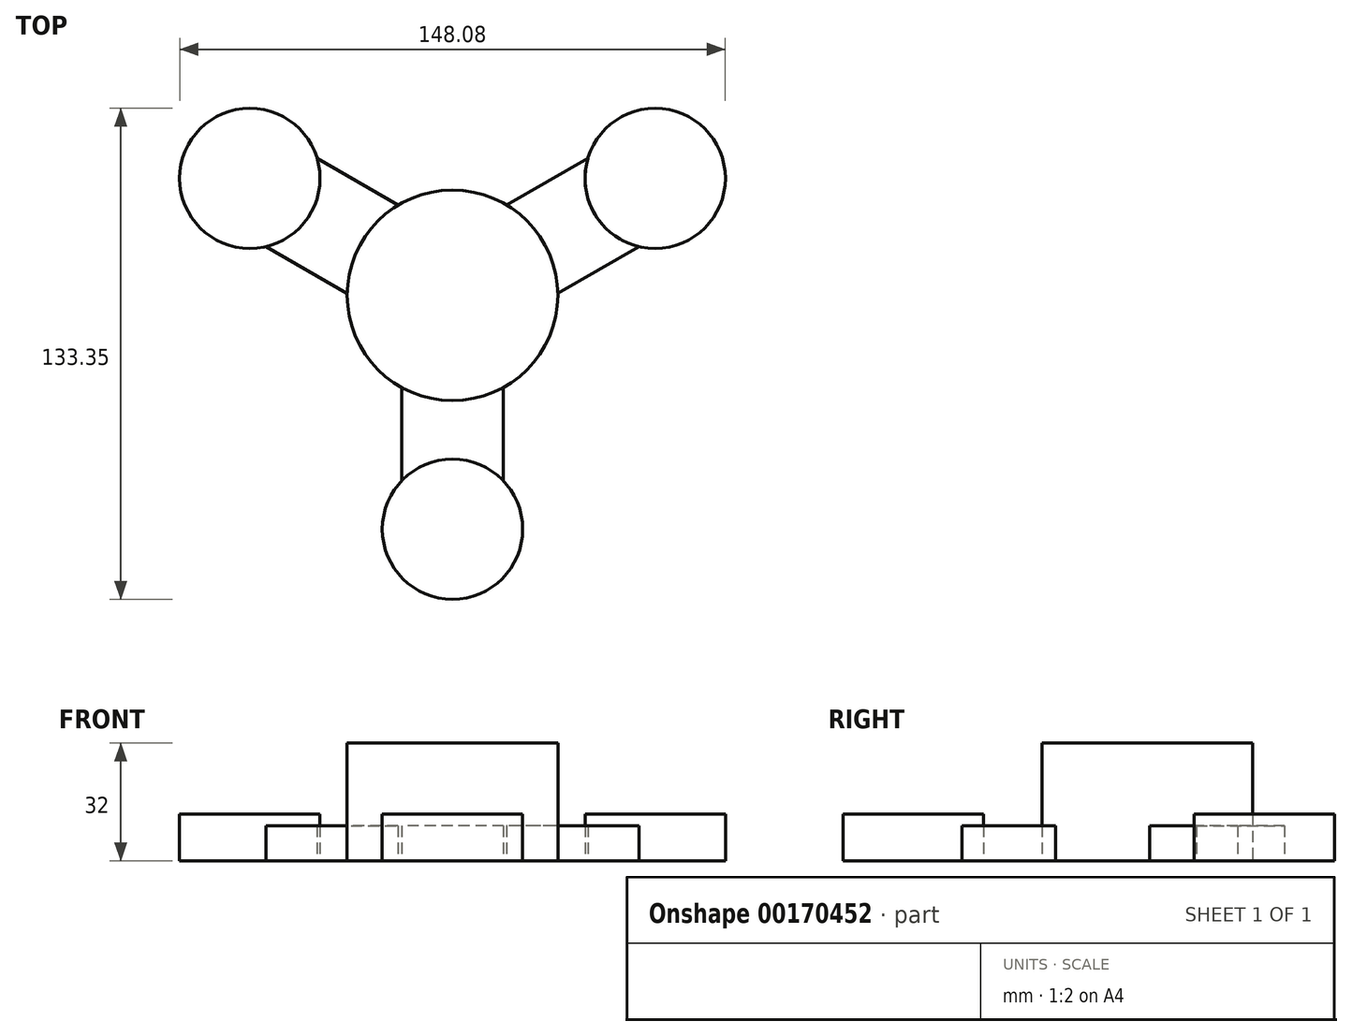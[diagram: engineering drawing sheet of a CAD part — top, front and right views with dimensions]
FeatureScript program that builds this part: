
annotation { "Feature Type Name" : "Feature", "Feature Type Description" : "" }
export const myFeature = defineFeature(function(context is Context, id is Id, definition is map)
    precondition{}
    {
        {
            var Q0;
            Q0=qCreatedBy(makeId("Top.planeOp"),FACE);
            var sketch = newSketch(context, id + "F0", { "sketchPlane" : qUnion([Q0])});
            skCircle(sketch, "E0", {"center": v(0, 0) * mm, "radius": 28.58 * mm});
            skLineSegment(sketch, "E1", {"start": v(0, 0) * mm, "end": v(-55, 31.75) * mm});
            skCircle(sketch, "E2", {"center": v(-55, 31.75) * mm, "radius": 19.05 * mm});
            skLineSegment(sketch, "E3", {"start": v(-55, 31.75) * mm, "end": v(-64.52, 15.25) * mm});
            skLineSegment(sketch, "E4", {"start": v(-55, 31.75) * mm, "end": v(-45.47, 48.25) * mm});
            skLineSegment(sketch, "E5", {"start": v(-36.73, 37.18) * mm, "end": v(-14.74, 24.48) * mm});
            skLineSegment(sketch, "E6.MirrorCS", {"start": v(-50.57, 13.22) * mm, "end": v(-28.57, 0.52) * mm});
            skSolve(sketch);
        }
        {
            var Q0;
            {var subQ0=sQuery(id+"F0.wireOp",EDGE,"E3");Q0=makeQuery(id+"F0.imprint","IMPRINT",FACE,{"disambiguationData":[TD([[makeQuery(id+"F0.imprint","IMPRINT",EDGE,{"derivedFrom":subQ0}),-1.0]])]});}
            var Q1;
            {var subQ0=sQuery(id+"F0.wireOp",EDGE,"E4");Q1=makeQuery(id+"F0.imprint","IMPRINT",FACE,{"disambiguationData":[TD([[makeQuery(id+"F0.imprint","IMPRINT",EDGE,{"derivedFrom":subQ0}),-1.0]])]});}
            var Q2;
            {var subQ0=sQuery(id+"F0.wireOp",EDGE,"E3");Q2=makeQuery(id+"F0.imprint","IMPRINT",FACE,{"disambiguationData":[TD([[makeQuery(id+"F0.imprint","IMPRINT",EDGE,{"derivedFrom":subQ0}),1.0]])]});}
            extrude(context, id + "F1", {"entities" : qUnion([Q0, Q1, Q2]), "depth" : 12.7 * mm, "offsetDistance" : 25.4 * mm});
        }
        {
            var Q0;
            {var subQ0=sQuery(id+"F0.wireOp",EDGE,"E0");var subQ1=makeQuery(id+"F0.imprint","INTERSECT",VERTEX,{"derivedFrom":[subQ0,sQuery(id+"F0.wireOp",EDGE,"E5")]});Q0=makeQuery(id+"F0.imprint","IMPRINT",FACE,{"disambiguationData":[TD([[makeQuery(id+"F0.imprint","IMPRINT",EDGE,{"disambiguationData":[TD([[subQ1,-1.0]])],"derivedFrom":subQ0}),1.0]])]});}
            extrude(context, id + "F2", {"entities" : qUnion([Q0]), "depth" : 19.05 * mm, "offsetDistance" : 25.4 * mm});
        }
        {
            var Q0;
            {var subQ0=sQuery(id+"F0.wireOp",EDGE,"E5");Q0=makeQuery(id+"F0.imprint","IMPRINT",FACE,{"disambiguationData":[TD([[makeQuery(id+"F0.imprint","IMPRINT",EDGE,{"derivedFrom":subQ0}),-1.0]])]});}
            var Q1;
            {var subQ0=sQuery(id+"F0.wireOp",EDGE,"E6.MirrorCS");Q1=makeQuery(id+"F0.imprint","IMPRINT",FACE,{"disambiguationData":[TD([[makeQuery(id+"F0.imprint","IMPRINT",EDGE,{"derivedFrom":subQ0}),1.0]])]});}
            extrude(context, id + "F3", {"entities" : qUnion([Q0, Q1]), "depth" : 9.52 * mm, "offsetDistance" : 25.4 * mm});
        }
        {
            var Q0;
            Q0=makeQuery(id+"F1.opExtrude","SWEPT_BODY",BODY,{"disambiguationData":[OSD([sQuery(id+"F0.wireOp",EDGE,"E2")])]});
            var Q1;
            Q1=makeQuery(id+"F3.opExtrude","SWEPT_BODY",BODY,{"disambiguationData":[OSD([sQuery(id+"F0.wireOp",EDGE,"E0"),sQuery(id+"F0.wireOp",EDGE,"E2"),sQuery(id+"F0.wireOp",EDGE,"E5"),sQuery(id+"F0.wireOp",EDGE,"E6.MirrorCS")])]});
            var Q2;
            Q2=makeQuery(id+"F2.opExtrude","CAP_EDGE",EDGE,{"disambiguationData":[OSD([sQuery(id+"F0.wireOp",EDGE,"E0")])],"isStart":false});
            circularPattern(context, id + "F4", {"entities" : qUnion([Q0, Q1]), "axis" : qUnion([Q2]), "angle" : 360 * degree, "instanceCount" : 3, "equalSpace" : true});
        }
        {
            var Q0;
            Q0=makeQuery(id+"F2.opExtrude","CAP_FACE",FACE,{"disambiguationData":[OSD([sQuery(id+"F0.wireOp",EDGE,"E0")])],"isStart":false});
            extrude(context, id + "F5", {"entities" : qUnion([Q0]), "operationType" : NewBodyOperationType.ADD, "depth" : 12.95 * mm, "offsetDistance" : 25.4 * mm});
        }
    });
